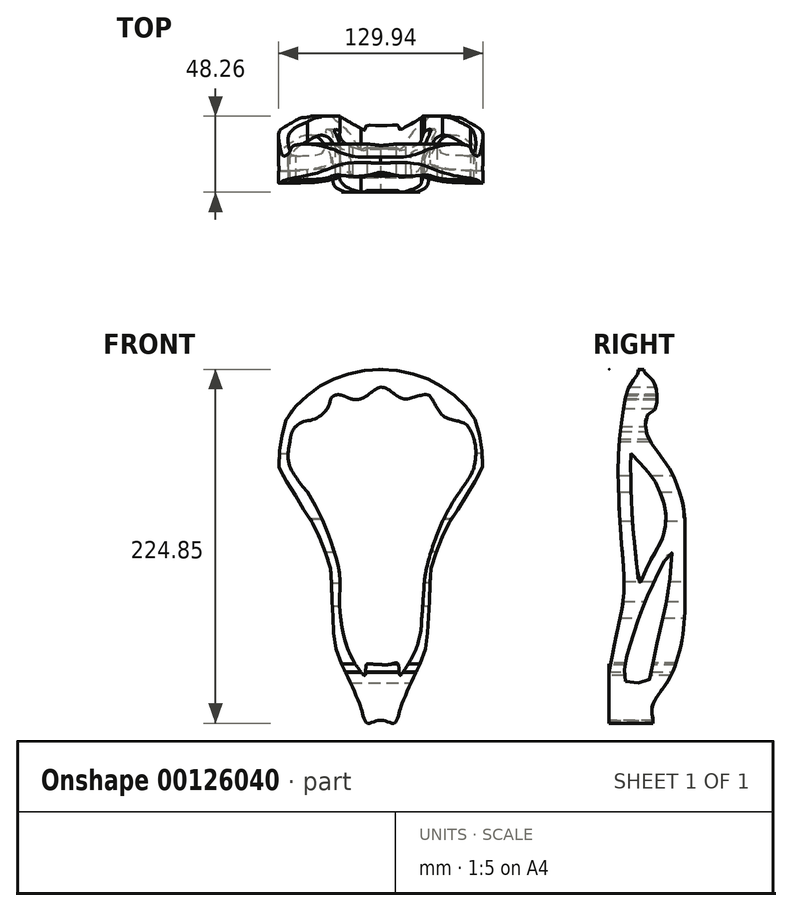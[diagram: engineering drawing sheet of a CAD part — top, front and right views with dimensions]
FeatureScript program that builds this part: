
annotation { "Feature Type Name" : "Feature", "Feature Type Description" : "" }
export const myFeature = defineFeature(function(context is Context, id is Id, definition is map)
    precondition{}
    {
        {
            var Q0;
            Q0=qCreatedBy(makeId("Front.planeOp"),FACE);
            var sketch = newSketch(context, id + "F0", { "sketchPlane" : qUnion([Q0])});
            skLineSegment(sketch, "E0", {"start": v(0, -72.83) * mm, "end": v(0, 150.24) * mm});
            skFitSpline(sketch, "E1", {"points": [v(0, 150.24) * mm, v(-1.48, 150.24) * mm, v(-4.3, 149.98) * mm, v(-9.4, 149.6) * mm, v(-12.84, 149.07) * mm, v(-16.02, 148.38) * mm, v(-20, 147.46) * mm, v(-25.8, 145.73) * mm, v(-31.7, 143.15) * mm, v(-37.82, 139.93) * mm, v(-51.56, 129.32) * mm, v(-60.43, 117.15) * mm, v(-64.43, 97.23) * mm, v(-64.26, 86.62) * mm, v(-56.78, 74.44) * mm, v(-49.65, 62.1) * mm, v(-45.82, 57.27) * mm, v(-39.73, 45.1) * mm, v(-34.34, 31.7) * mm, v(-31.9, 23.35) * mm, v(-31.04, 8.22) * mm, v(-30.34, -6.4) * mm, v(-28.43, -27.02) * mm, v(-20.77, -45.63) * mm, v(-13.64, -61.98) * mm, v(-11.9, -67.02) * mm, v(-10.34, -72.06) * mm, v(-8.43, -74.5) * mm, v(-4.95, -73.8) * mm, v(-1.64, -72.76) * mm, v(0, -72.83) * mm], "startDerivative": vector(-100.07, 3.17) * mm, "endDerivative": vector(103.4, -15.38) * mm});
            skSolve(sketch);
        }
        {
            var Q0;
            Q0=makeQuery(id+"F0.imprint","IMPRINT",FACE,{"disambiguationData":[TD([[makeQuery(id+"F0.imprint","IMPRINT",EDGE,{"derivedFrom":sQuery(id+"F0.wireOp",EDGE,"E0")}),1.0]])]});
            extrude(context, id + "F1", {"entities" : qUnion([Q0]), "oppositeDirection" : true, "depth" : 48.26 * mm});
        }
        {
            var Q0;
            Q0=makeQuery(id+"F1.opExtrude","SWEPT_BODY",BODY,{"disambiguationData":[OSD([sQuery(id+"F0.wireOp",EDGE,"E0"),sQuery(id+"F0.wireOp",EDGE,"E1")])]});
            var Q1;
            Q1=qCreatedBy(makeId("Right.planeOp"),FACE);
            mirror(context, id + "F2", {"operationType" : NewBodyOperationType.ADD, "entities" : qUnion([Q0]), "mirrorPlane" : qUnion([Q1])});
        }
        {
            var Q0;
            Q0=qCreatedBy(makeId("Right.planeOp"),FACE);
            var sketch = newSketch(context, id + "F3", { "sketchPlane" : qUnion([Q0])});
            skFitSpline(sketch, "E2", {"points": [v(0, -42.42) * mm, v(5.3, -15.25) * mm, v(8.62, 0) * mm, v(9.61, 14.25) * mm, v(7.95, 40.43) * mm, v(6.3, 64.3) * mm, v(6.05, 74.12) * mm, v(5.88, 81.69) * mm, v(5.88, 93.93) * mm, v(6.31, 104) * mm, v(8.94, 124.32) * mm, v(13.96, 141.36) * mm, v(18.55, 150.1) * mm, v(0, 150.26) * mm, v(0, -36.86) * mm, v(0, -42.42) * mm]});
            skSolve(sketch);
        }
        {
            var Q0;
            Q0=makeQuery(id+"F3.imprint","IMPRINT",FACE,{"disambiguationData":[TD([[makeQuery(id+"F3.imprint","IMPRINT",EDGE,{"derivedFrom":sQuery(id+"F3.wireOp",EDGE,"E2")}),1.0]])]});
            extrude(context, id + "F4", {"entities" : qUnion([Q0]), "operationType" : NewBodyOperationType.REMOVE, "endBound" : BoundingType.SYMMETRIC, "depth" : 152.4 * mm});
        }
        {
            var Q0;
            Q0=qCreatedBy(makeId("Right.planeOp"),FACE);
            var sketch = newSketch(context, id + "F5", { "sketchPlane" : qUnion([Q0])});
            skFitSpline(sketch, "E3", {"points": [v(10.32, -47.88) * mm, v(24.23, -48.44) * mm, v(25.9, -46.5) * mm, v(30.62, -23.4) * mm, v(37.02, 5.8) * mm, v(39.25, 24.16) * mm, v(39.53, 34.17) * mm, v(32.3, 22.77) * mm, v(20.8, -2.5) * mm, v(16.03, -16.67) * mm, v(13.18, -25.3) * mm, v(10.15, -38.42) * mm, v(9.43, -46.35) * mm, v(10.32, -47.88) * mm]});
            skSolve(sketch);
        }
        {
            var Q0;
            Q0=qSketchRegion(id+"F5",true);
            extrude(context, id + "F6", {"entities" : qUnion([Q0]), "operationType" : NewBodyOperationType.REMOVE, "endBound" : BoundingType.SYMMETRIC, "oppositeDirection" : true, "depth" : 127 * mm});
        }
        {
            var Q0;
            Q0=qCreatedBy(makeId("Right.planeOp"),FACE);
            var sketch = newSketch(context, id + "F7", { "sketchPlane" : qUnion([Q0])});
            skFitSpline(sketch, "E4", {"points": [v(13.88, 96.8) * mm, v(13.72, 83.36) * mm, v(14.2, 67.88) * mm, v(15.62, 45.6) * mm, v(17.51, 27.12) * mm, v(19.25, 14.55) * mm, v(21.78, 19.3) * mm, v(28.89, 33.2) * mm, v(34.1, 43.3) * mm, v(36.16, 55) * mm, v(34.26, 67) * mm, v(27.78, 81.38) * mm, v(22.4, 87.86) * mm, v(16.09, 94.97) * mm, v(14.62, 96.3) * mm, v(13.88, 96.8) * mm]});
            skSolve(sketch);
        }
        {
            var Q0;
            Q0=qSketchRegion(id+"F7",true);
            extrude(context, id + "F8", {"entities" : qUnion([Q0]), "operationType" : NewBodyOperationType.REMOVE, "endBound" : BoundingType.SYMMETRIC, "depth" : 152.4 * mm});
        }
        {
            var Q0;
            Q0=qCreatedBy(makeId("Right.planeOp"),FACE);
            var sketch = newSketch(context, id + "F9", { "sketchPlane" : qUnion([Q0])});
            skFitSpline(sketch, "E5", {"points": [v(48.29, 55.32) * mm, v(47.36, 62.26) * mm, v(44.82, 71.9) * mm, v(39.67, 84.9) * mm, v(28.84, 100.6) * mm, v(23.15, 112.51) * mm, v(25.05, 121.72) * mm, v(28.57, 123.88) * mm, v(30.47, 134.44) * mm, v(26.4, 144.73) * mm, v(22.34, 150.42) * mm, v(48.6, 150.15) * mm, v(48.29, 55.32) * mm]});
            skSolve(sketch);
        }
        {
            var Q0;
            Q0=makeQuery(id+"F9.imprint","IMPRINT",FACE,{"disambiguationData":[TD([[makeQuery(id+"F9.imprint","IMPRINT",EDGE,{"derivedFrom":sQuery(id+"F9.wireOp",EDGE,"E5")}),-1.0]])]});
            extrude(context, id + "F10", {"entities" : qUnion([Q0]), "operationType" : NewBodyOperationType.REMOVE, "endBound" : BoundingType.SYMMETRIC, "depth" : 152.4 * mm});
        }
        {
            var Q0;
            Q0=qCreatedBy(makeId("Front.planeOp"),FACE);
            var sketch = newSketch(context, id + "F11", { "sketchPlane" : qUnion([Q0])});
            skFitSpline(sketch, "E6", {"points": [v(-10.62, -43.3) * mm, v(-13.07, -41.28) * mm, v(-19.85, -30.03) * mm, v(-25.62, -6.52) * mm, v(-26, 10.22) * mm, v(-26.44, 21.57) * mm, v(-33.81, 46.75) * mm, v(-47.27, 73.22) * mm, v(-56.82, 88.41) * mm, v(-57.69, 104.47) * mm, v(-54.21, 113.59) * mm, v(-42.5, 117.93) * mm, v(-35.12, 121.84) * mm, v(-30.78, 131.38) * mm, v(-29.28, 133.67) * mm, v(-25.34, 133.9) * mm, v(-18.32, 131.3) * mm, v(-11.62, 131.94) * mm, v(-3.82, 136.9) * mm, v(-0.66, 138.56) * mm, v(2.17, 138.4) * mm, v(7.77, 135.09) * mm, v(14.01, 131.62) * mm, v(20, 131.86) * mm, v(26.62, 133.83) * mm, v(29.38, 133.99) * mm, v(31.98, 131.94) * mm, v(36, 125.16) * mm, v(40.26, 120.27) * mm, v(46.88, 117.9) * mm, v(53.95, 115.38) * mm, v(57.73, 109.87) * mm, v(60.18, 101.27) * mm, v(59.86, 91.26) * mm, v(57.02, 82.9) * mm, v(46.78, 67.75) * mm, v(39.84, 55.06) * mm, v(36.6, 47.65) * mm, v(29.78, 26.78) * mm, v(27.16, 9.45) * mm, v(26.33, -4.68) * mm, v(24.2, -16.2) * mm, v(16.23, -37.04) * mm, v(12.52, -43.53) * mm, v(11.6, -36.42) * mm, v(10.36, -33.33) * mm, v(-7.55, -33.33) * mm, v(-10.62, -43.3) * mm]});
            skSolve(sketch);
        }
        {
            var Q0;
            Q0=makeQuery(id+"F11.imprint","IMPRINT",FACE,{"disambiguationData":[TD([[makeQuery(id+"F11.imprint","IMPRINT",EDGE,{"derivedFrom":sQuery(id+"F11.wireOp",EDGE,"E6")}),-1.0]])]});
            extrude(context, id + "F12", {"entities" : qUnion([Q0]), "operationType" : NewBodyOperationType.REMOVE, "endBound" : BoundingType.SYMMETRIC, "depth" : 228.6 * mm});
        }
        {
            var Q0;
            Q0=qCreatedBy(makeId("Front.planeOp"),FACE);
            var sketch = newSketch(context, id + "F13", { "sketchPlane" : qUnion([Q0])});
            skFitSpline(sketch, "E7", {"points": [v(12.08, -44) * mm, v(14.73, -41.19) * mm, v(19.87, -32.9) * mm, v(25.01, -18.46) * mm, v(26.18, -4.7) * mm, v(27.2, 7.62) * mm, v(27.97, 18.2) * mm, v(31.56, 35.9) * mm, v(38.5, 52.33) * mm, v(48.5, 70.03) * mm, v(57.99, 84.9) * mm, v(60.1, 96.01) * mm, v(59.08, 106.28) * mm, v(54.2, 114.49) * mm, v(44.45, 118.34) * mm, v(39.32, 120.64) * mm, v(36.5, 124.24) * mm, v(31.37, 132.96) * mm, v(28.55, 134.24) * mm, v(21.88, 132.7) * mm, v(14.44, 131.42) * mm, v(7.77, 135.27) * mm, v(0, 138.86) * mm, v(-8.4, 133.73) * mm, v(-15.84, 130.9) * mm, v(-23.54, 133.22) * mm, v(-28.4, 133.99) * mm, v(-31.49, 131.93) * mm, v(-32.77, 127.83) * mm, v(-36.36, 122.44) * mm, v(-43.03, 118.34) * mm, v(-50.22, 116.54) * mm, v(-55.6, 111.4) * mm, v(-58.17, 101.66) * mm, v(-58.17, 89.6) * mm, v(-47.14, 72.92) * mm, v(-38.67, 60.35) * mm, v(-30.46, 40.6) * mm, v(-24.82, 15.97) * mm, v(-22.77, -13.54) * mm, v(-16.6, -32.78) * mm, v(-11.99, -42.79) * mm, v(-9.94, -44.07) * mm, v(-8.91, -36.89) * mm, v(-5.58, -36.89) * mm, v(-2.24, -37.14) * mm, v(5.97, -37.14) * mm, v(10.84, -36.63) * mm, v(12.08, -44) * mm]});
            skSolve(sketch);
        }
        {
            var Q0;
            Q0=makeQuery(id+"F13.imprint","IMPRINT",FACE,{"disambiguationData":[TD([[makeQuery(id+"F13.imprint","IMPRINT",EDGE,{"derivedFrom":sQuery(id+"F13.wireOp",EDGE,"E7")}),1.0]])]});
            extrude(context, id + "F14", {"entities" : qUnion([Q0]), "operationType" : NewBodyOperationType.REMOVE, "endBound" : BoundingType.SYMMETRIC, "depth" : 228.6 * mm});
        }
        {
            var Q0;
            Q0=qCreatedBy(makeId("Right.planeOp"),FACE);
            var sketch = newSketch(context, id + "F15", { "sketchPlane" : qUnion([Q0])});
            skFitSpline(sketch, "E8", {"points": [v(48.25, -0.25) * mm, v(48.37, -74.61) * mm, v(28, -74.61) * mm, v(28.06, -73.94) * mm, v(27.6, -70.58) * mm, v(27.19, -66.2) * mm, v(27.8, -62.78) * mm, v(31.96, -55.58) * mm, v(36.87, -48.65) * mm, v(40.5, -41.86) * mm, v(42.46, -37.02) * mm, v(45.28, -26.91) * mm, v(46.7, -19.31) * mm, v(47.97, -6.06) * mm, v(48.24, -2.3) * mm, v(48.25, -0.25) * mm]});
            skSolve(sketch);
        }
        {
            var Q0;
            Q0=qSketchRegion(id+"F15",true);
            extrude(context, id + "F16", {"entities" : qUnion([Q0]), "operationType" : NewBodyOperationType.REMOVE, "endBound" : BoundingType.SYMMETRIC, "depth" : 228.6 * mm});
        }
    });
